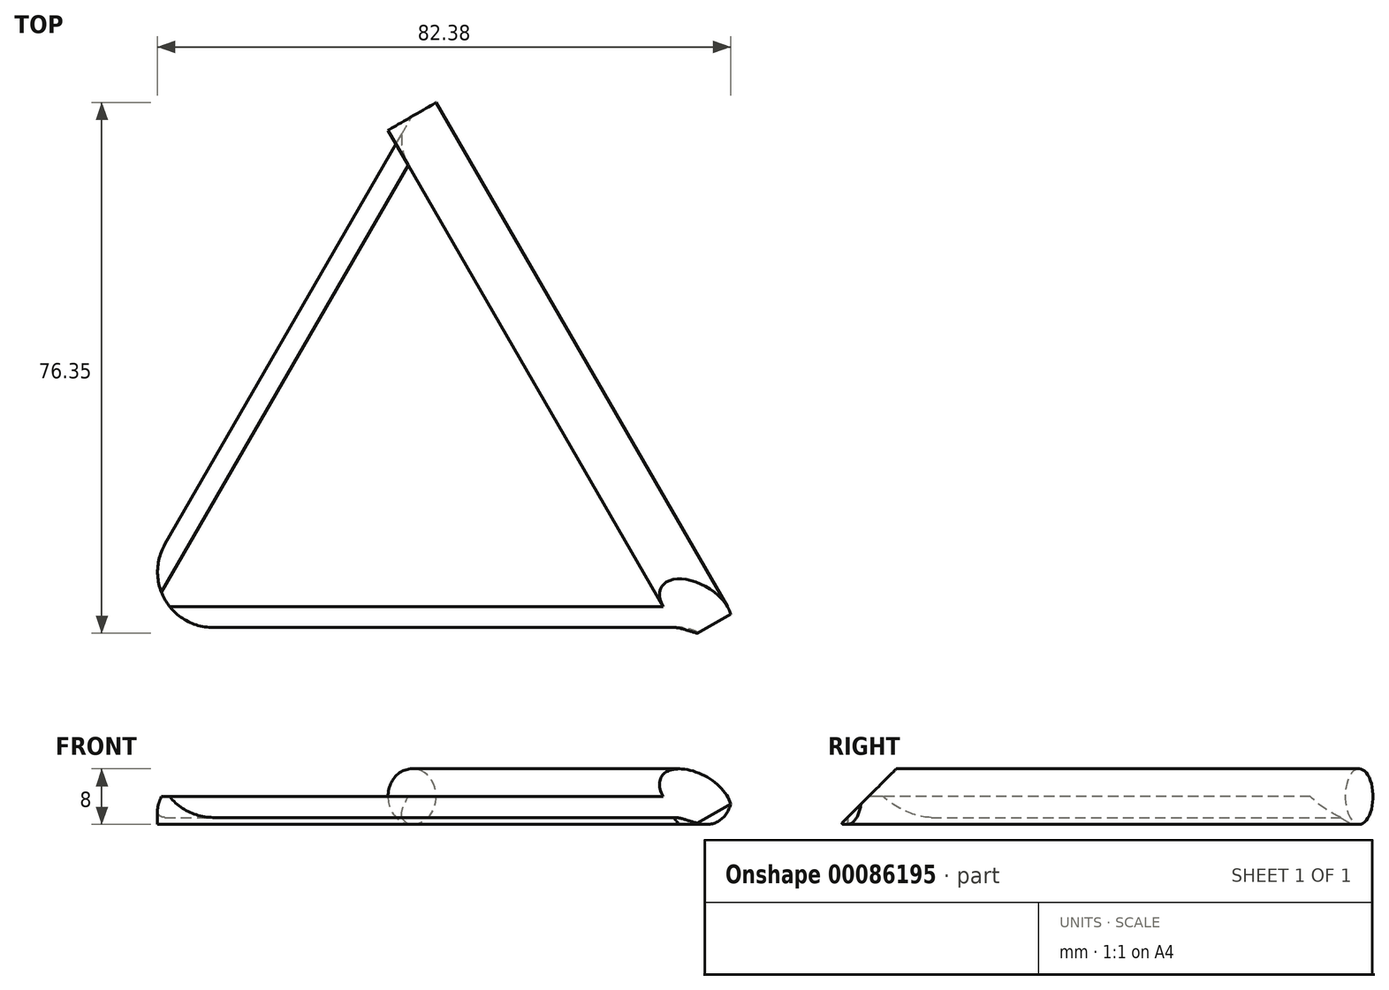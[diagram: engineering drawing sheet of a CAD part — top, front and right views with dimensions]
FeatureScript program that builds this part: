
annotation { "Feature Type Name" : "Feature", "Feature Type Description" : "" }
export const myFeature = defineFeature(function(context is Context, id is Id, definition is map)
    precondition{}
    {
        {
            assignVariable(context, id + "F0", {"name" : "thickness", "anyValue" : 4});
        }
        {
            var Q0;
            Q0=qCreatedBy(makeId("Top.planeOp"),FACE);
            var sketch = newSketch(context, id + "F1", { "sketchPlane" : qUnion([Q0])});
            skLineSegment(sketch, "E0", {"start": v(0, 0) * mm, "end": v(-35.52, -61.53) * mm});
            skLineSegment(sketch, "E1", {"start": v(-28.6, -73.53) * mm, "end": v(42.45, -73.53) * mm});
            skLineSegment(sketch, "E2", {"start": v(42.45, -73.53) * mm, "end": v(0, 0) * mm});
            skLineSegment(sketch, "E3", {"start": v(0, 0) * mm, "end": v(0, -73.53) * mm, "construction": true});
            skLineSegment(sketch, "E4", {"start": v(-42.45, -73.53) * mm, "end": v(21.23, -36.76) * mm, "construction": true});
            skLineSegment(sketch, "E5", {"start": v(42.45, -73.53) * mm, "end": v(-21.23, -36.76) * mm, "construction": true});
            skPoint(sketch, "E6.visualSharp", {"position": v(-42.45, -73.53) * mm});
            skArc(sketch, "E6.filletArc", {"start": v(-35.52, -61.53) * mm, "mid": v(-35.52, -69.53) * mm, "end": v(-28.6, -73.53) * mm});
            skSolve(sketch);
        }
        {
            var Q0;
            Q0=makeQuery(id+"F1.imprint","IMPRINT",FACE,{"disambiguationData":[TD([[makeQuery(id+"F1.imprint","IMPRINT",EDGE,{"derivedFrom":sQuery(id+"F1.wireOp",EDGE,"E0")}),1.0]])]});
            extrude(context, id + "F2", {"entities" : qUnion([Q0]), "depth" : (getVariable(context, 'thickness')) * mm, "offsetDistance" : 25 * mm});
        }
        {
            var Q0;
            Q0=makeQuery(id+"F2.opExtrude","SWEPT_FACE",FACE,{"disambiguationData":[OSD([sQuery(id+"F1.wireOp",EDGE,"E2")])]});
            var Q1;
            Q1=makeQuery(id+"F2.opExtrude","CAP_EDGE",EDGE,{"disambiguationData":[OSD([sQuery(id+"F1.wireOp",EDGE,"E2")])],"isStart":false});
            revolve(context, id + "F3", {"operationType" : NewBodyOperationType.ADD, "entities" : qUnion([Q0]), "axis" : qUnion([Q1]), "revolveType" : RevolveType.FULL});
        }
        {
            var Q0;
            Q0=makeQuery(id+"F3.boolean.opBoolean","INTERSECT",EDGE,{"derivedFrom":[makeQuery(id+"F2.opExtrude","SWEPT_FACE",FACE,{"disambiguationData":[OSD([sQuery(id+"F1.wireOp",EDGE,"E1")])]}),makeQuery(id+"F3.opRevolve","SWEPT_FACE",FACE,{"disambiguationData":[OSD([sQuery(id+"F1.wireOp",EDGE,"E2")])]})]});
            fillet(context, id + "F4", {"entities" : qUnion([Q0]), "radius" : 2 * mm, "tangentPropagation" : true, "allowEdgeOverflow" : false});
        }
        {
            var Q0;
            Q0=makeQuery(id+"F2.opExtrude","CAP_EDGE",EDGE,{"disambiguationData":[OSD([sQuery(id+"F1.wireOp",EDGE,"E1")])],"isStart":false});
            var Q1;
            Q1=makeQuery(id+"F2.opExtrude","CAP_EDGE",EDGE,{"disambiguationData":[OSD([sQuery(id+"F1.wireOp",EDGE,"E0")])],"isStart":false});
            chamfer(context, id + "F5", {"entities" : qUnion([Q0, Q1]), "width" : 3 * mm});
        }
    });
